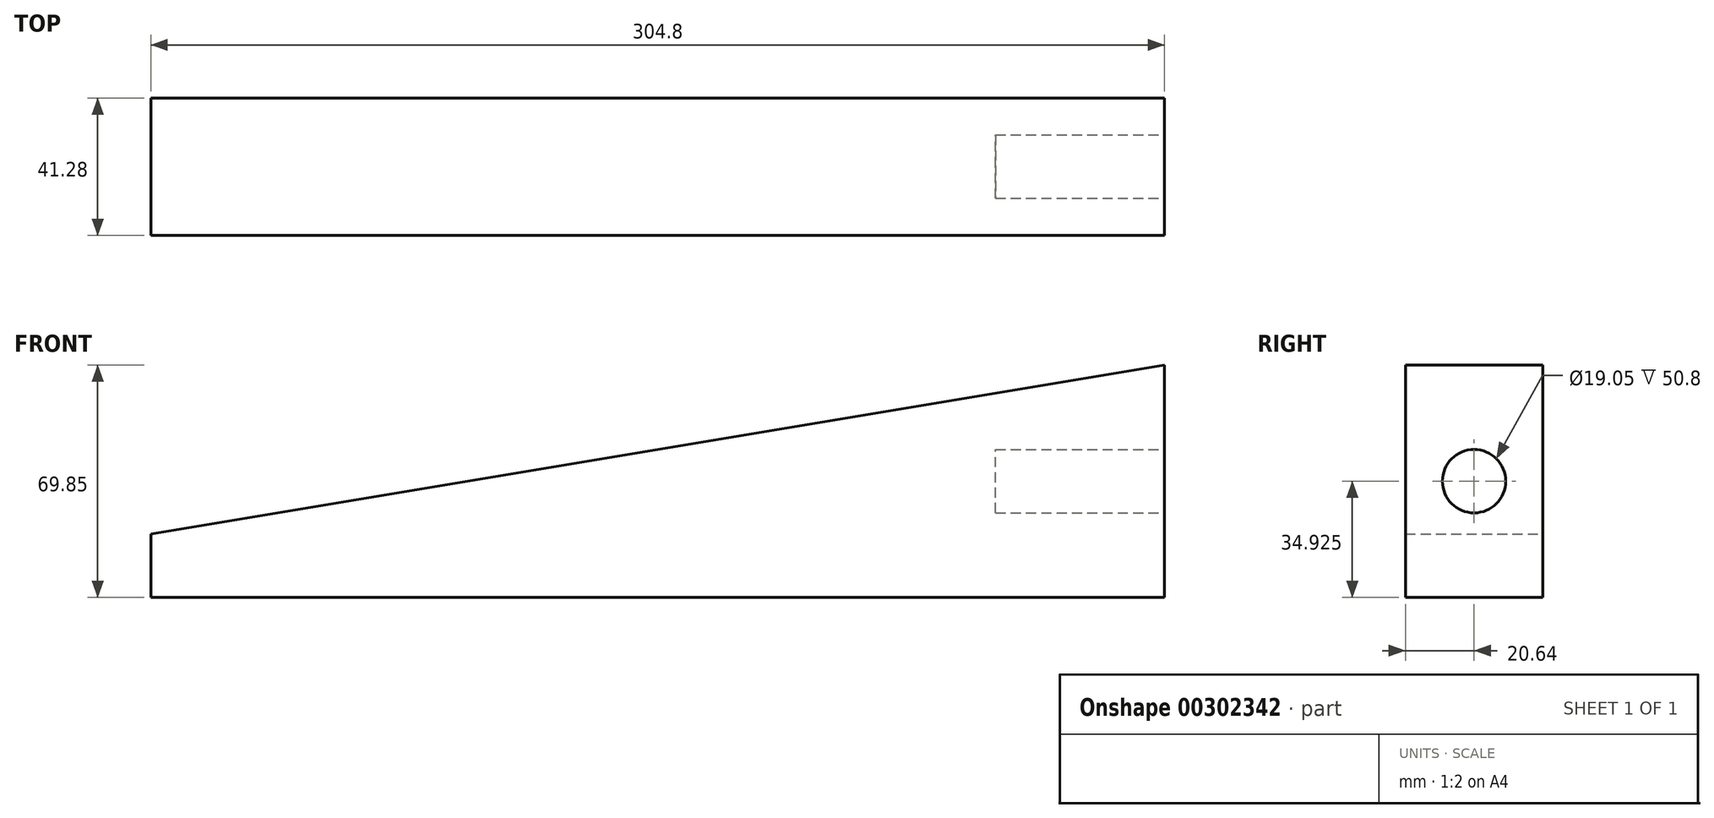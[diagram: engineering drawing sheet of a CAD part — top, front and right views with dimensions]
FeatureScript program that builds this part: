
annotation { "Feature Type Name" : "Feature", "Feature Type Description" : "" }
export const myFeature = defineFeature(function(context is Context, id is Id, definition is map)
    precondition{}
    {
        {
            var Q0;
            Q0=qCreatedBy(makeId("Front.planeOp"),FACE);
            var sketch = newSketch(context, id + "F0", { "sketchPlane" : qUnion([Q0])});
            skLineSegment(sketch, "E0", {"start": v(0, 0) * mm, "end": v(-304.8, 0) * mm});
            skLineSegment(sketch, "E1", {"start": v(0, 0) * mm, "end": v(0, 69.85) * mm});
            skLineSegment(sketch, "E2", {"start": v(-304.8, 0) * mm, "end": v(-304.8, 19.05) * mm});
            skLineSegment(sketch, "E3", {"start": v(0, 69.85) * mm, "end": v(-304.8, 19.05) * mm});
            skSolve(sketch);
        }
        {
            var Q0;
            Q0=qCreatedBy(makeId("Right.planeOp"),FACE);
            var sketch = newSketch(context, id + "F1", { "sketchPlane" : qUnion([Q0])});
            skCircle(sketch, "E4", {"center": v(0, 34.93) * mm, "radius": 9.53 * mm});
            skSolve(sketch);
        }
        {
            var Q0;
            Q0 = qSketchRegion(id + "F0", true);
            extrude(context, id + "F2", {"entities" : qUnion([Q0]), "depth" : 41.27 * mm, "offsetDistance" : 25.4 * mm, "symmetric" : true});
        }
        {
            var Q0;
            Q0 = qSketchRegion(id + "F1", true);
            extrude(context, id + "F3", {"entities" : qUnion([Q0]), "operationType" : NewBodyOperationType.REMOVE, "oppositeDirection" : true, "depth" : 50.8 * mm, "offsetDistance" : 25.4 * mm});
        }
    });
